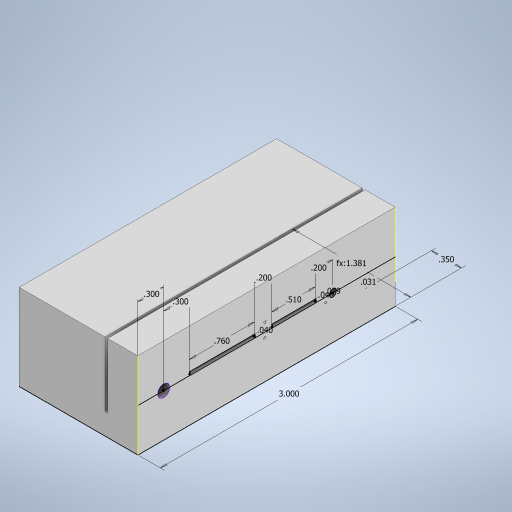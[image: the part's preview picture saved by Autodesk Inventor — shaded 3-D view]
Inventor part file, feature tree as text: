
AUTODESK INVENTOR PART (.ipt)
format: ipt  version: 2023 (Build 270158000, 158)  size: 262,656 bytes
history: native  units: in
note: dims shown in document units (in); Inventor stores cm internally (conversion verified against a paired STEP export)
features: extrude x6, sketch x2
ambient origin geometry x8: Origin, YZ Plane, XZ Plane, XY Plane, X Axis, Y Axis, Z Axis, Center Point
bodies: Solid1 (feature_tree)
feature tree (8):
  sketch  "Sketch1"  dims[d1=3.0in d2=1.3815in]
  extrude  "Extrusion1"  Depth=1.3815in
  extrude  "Extrusion2"  Depth=0.0315in
  extrude  "Extrusion3"  Depth=0.25in TaperAngle=0.0deg
  sketch  "Sketch2"  dims[d3=0.35in d4=0.0315in d5=0.25in d6=0.0in d7=1.0in d8=0.0in d9=1.0in d10=0.0in d11=1.1215in d12=0.0in d13=0.76in d14=0.04in d15=0.51in d16=0.04in d17=1.1015in d18=0.0in d19=0.079in d20=0.7315in d21=0.0in d22=0.3in d23=0.3in d24=0.2in d25=0.2in]
  extrude  "Extrusion4"  Depth=1.0in TaperAngle=0.0deg
  extrude  "Extrusion5"  Depth=1.0in TaperAngle=0.0deg
  extrude  "Extrusion6"  Depth=1.1215in
